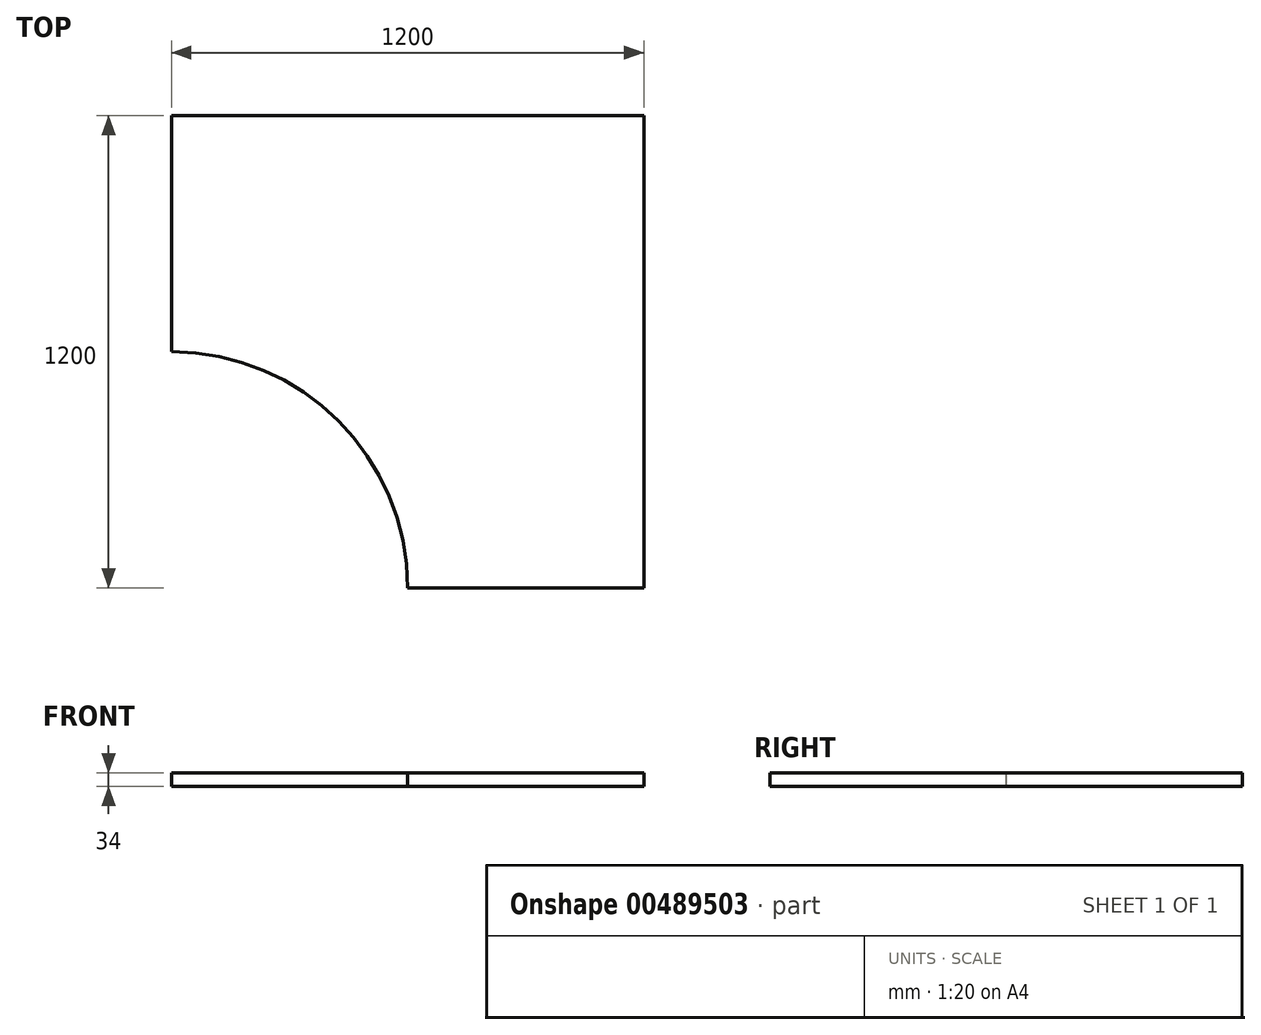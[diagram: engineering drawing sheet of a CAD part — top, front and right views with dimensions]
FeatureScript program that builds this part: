
annotation { "Feature Type Name" : "Feature", "Feature Type Description" : "" }
export const myFeature = defineFeature(function(context is Context, id is Id, definition is map)
    precondition{}
    {
        {
            var Q0;
            Q0=qCreatedBy(makeId("Top.planeOp"),FACE);
            var sketch = newSketch(context, id + "F0", { "sketchPlane" : qUnion([Q0])});
            skLineSegment(sketch, "E0", {"start": v(0, 0) * mm, "end": v(-1200, 0) * mm});
            skLineSegment(sketch, "E1", {"start": v(-1200, 0) * mm, "end": v(-1200, -600) * mm});
            skLineSegment(sketch, "E2", {"start": v(0, 0) * mm, "end": v(0, -1200) * mm});
            skLineSegment(sketch, "E3", {"start": v(0, -1200) * mm, "end": v(-600, -1200) * mm});
            skArc(sketch, "E4", {"start": v(-600, -1200) * mm, "mid": v(-775.74, -775.74) * mm, "end": v(-1200, -600) * mm});
            skSolve(sketch);
        }
        {
            var Q0;
            Q0 = qSketchRegion(id + "F0", true);
            extrude(context, id + "F1", {"entities" : qUnion([Q0]), "depth" : 34 * mm});
        }
    });
